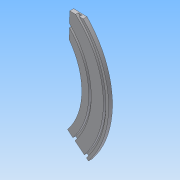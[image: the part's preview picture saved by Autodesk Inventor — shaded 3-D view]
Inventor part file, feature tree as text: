
AUTODESK INVENTOR PART (.ipt)
format: ipt  version: 2013 (Build 170138000, 138)  size: 147,968 bytes
history: native  units: in
note: dims shown in document units (in); Inventor stores cm internally (conversion verified against a paired STEP export)
features: extrude x2, plane x1, other x1, reference x1, sketch x1
ambient origin geometry x8: Origin, YZ Plane, XZ Plane, XY Plane, X Axis, Y Axis, Z Axis, Center Point
feature tree (6):
  plane  "Work Plane1"
  extrude  "Extrusion3"  Depth=2.5in
  extrude  "Extrusion4"  Depth=2.5in
  other  "ThermoBulbBorder"
  reference  "Reference2"
  sketch  "Sketch2"  dims[d0=24.0in d5=2.5in d6=2.5in d7=33.0in d8=0.32in d9=0.32in d10=2.25in d11=1.61in d12=6.0in d15=0.71in d16=0.0in d17=0.5in d19=0.48in d20=2.25in d21=0.5in d22=0.0in d23=0.5in d24=1.0in d25=0.48in]
